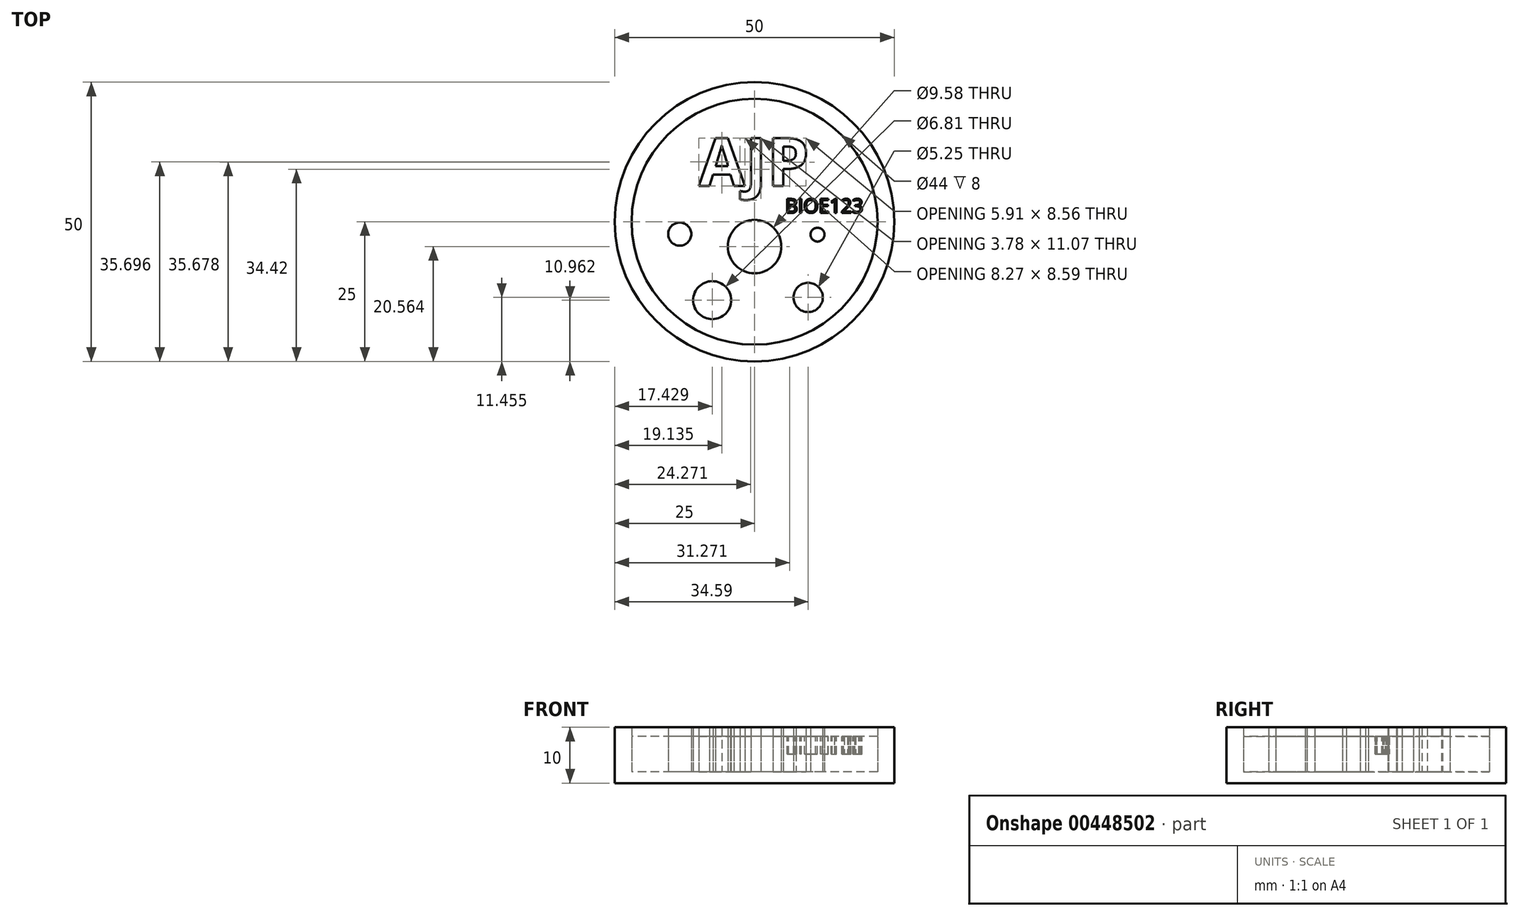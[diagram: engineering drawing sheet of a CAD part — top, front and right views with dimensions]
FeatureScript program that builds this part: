
annotation { "Feature Type Name" : "Feature", "Feature Type Description" : "" }
export const myFeature = defineFeature(function(context is Context, id is Id, definition is map)
    precondition{}
    {
        {
            var Q0;
            Q0=qCreatedBy(makeId("Top.planeOp"),FACE);
            var sketch = newSketch(context, id + "F0", { "sketchPlane" : qUnion([Q0])});
            skCircle(sketch, "E0", {"center": v(0, 0) * mm, "radius": 25 * mm});
            skCircle(sketch, "E1", {"center": v(0, 0) * mm, "radius": 22 * mm});
            skCircle(sketch, "E2", {"center": v(0, -4.44) * mm, "radius": 4.79 * mm});
            skCircle(sketch, "E3", {"center": v(-7.57, -14.04) * mm, "radius": 3.4 * mm});
            skCircle(sketch, "E4", {"center": v(9.6, -13.55) * mm, "radius": 2.63 * mm});
            skCircle(sketch, "E5", {"center": v(-13.39, -2.2) * mm, "radius": 2.07 * mm});
            skCircle(sketch, "E6", {"center": v(11.27, -2.3) * mm, "radius": 1.24 * mm});
            skSolve(sketch);
        }
        {
            var Q0;
            Q0=makeQuery(id+"F0.imprint","IMPRINT",FACE,{"disambiguationData":[TD([[makeQuery(id+"F0.imprint","IMPRINT",EDGE,{"derivedFrom":sQuery(id+"F0.wireOp",EDGE,"E0")}),1.0]])]});
            extrude(context, id + "F1", {"entities" : qUnion([Q0]), "depth" : 10 * mm});
        }
        {
            var Q0;
            Q0=makeQuery(id+"F0.imprint","IMPRINT",FACE,{"disambiguationData":[TD([[makeQuery(id+"F0.imprint","IMPRINT",EDGE,{"derivedFrom":sQuery(id+"F0.wireOp",EDGE,"E1")}),1.0]])]});
            extrude(context, id + "F2", {"entities" : qUnion([Q0]), "operationType" : NewBodyOperationType.ADD, "depth" : 2 * mm});
        }
        {
            var Q0;
            Q0=makeQuery(id+"F0.imprint","IMPRINT",FACE,{"disambiguationData":[TD([[makeQuery(id+"F0.imprint","IMPRINT",EDGE,{"derivedFrom":sQuery(id+"F0.wireOp",EDGE,"E5")}),1.0]])]});
            var Q1;
            Q1=makeQuery(id+"F0.imprint","IMPRINT",FACE,{"disambiguationData":[TD([[makeQuery(id+"F0.imprint","IMPRINT",EDGE,{"derivedFrom":sQuery(id+"F0.wireOp",EDGE,"E3")}),1.0]])]});
            var Q2;
            Q2=makeQuery(id+"F0.imprint","IMPRINT",FACE,{"disambiguationData":[TD([[makeQuery(id+"F0.imprint","IMPRINT",EDGE,{"derivedFrom":sQuery(id+"F0.wireOp",EDGE,"E2")}),1.0]])]});
            var Q3;
            Q3=makeQuery(id+"F0.imprint","IMPRINT",FACE,{"disambiguationData":[TD([[makeQuery(id+"F0.imprint","IMPRINT",EDGE,{"derivedFrom":sQuery(id+"F0.wireOp",EDGE,"E6")}),1.0]])]});
            var Q4;
            Q4=makeQuery(id+"F0.imprint","IMPRINT",FACE,{"disambiguationData":[TD([[makeQuery(id+"F0.imprint","IMPRINT",EDGE,{"derivedFrom":sQuery(id+"F0.wireOp",EDGE,"E4")}),1.0]])]});
            extrude(context, id + "F3", {"entities" : qUnion([Q0, Q1, Q2, Q3, Q4]), "operationType" : NewBodyOperationType.ADD, "depth" : 10 * mm});
        }
        {
            var Q0;
            Q0=qCreatedBy(makeId("Top.planeOp"),FACE);
            var sketch = newSketch(context, id + "F4", { "sketchPlane" : qUnion([Q0])});
            skText(sketch, "E7", { "text": "AJP", "fontName": "OpenSans-Bold.ttf"});
            const initialGuessF4  = {"E7": [-0.01, 0.0064, 1, 0, 0.00863]};
            skSetInitialGuess(sketch, initialGuessF4);
            skSolve(sketch);
        }
        {
            var Q0;
            Q0 = qSketchRegion(id + "F4", true);
            extrude(context, id + "F5", {"entities" : qUnion([Q0]), "operationType" : NewBodyOperationType.ADD, "depth" : 10 * mm});
        }
        {
            var Q0;
            {var subQ0=sQuery(id+"F0.wireOp",EDGE,"E6");var subQ1=sQuery(id+"F0.wireOp",EDGE,"E4");var subQ2=sQuery(id+"F0.wireOp",EDGE,"E3");var subQ3=sQuery(id+"F0.wireOp",EDGE,"E2");var subQ4=sQuery(id+"F0.wireOp",EDGE,"E1");var subQ5=sQuery(id+"F0.wireOp",EDGE,"E5");Q0=makeQuery(id+"F5.boolean.opBoolean","SPLIT",FACE,{"disambiguationData":[TD([makeQuery(id+"F1.opExtrude","SWEPT_FACE",FACE,{"disambiguationData":[OSD([subQ4])]})])],"derivedFrom":makeQuery(id+"F2.opExtrude","CAP_FACE",FACE,{"disambiguationData":[OSD([subQ4,subQ3,subQ2,subQ1,subQ5,subQ0])],"isStart":false})});}
            extrude(context, id + "F6", {"entities" : qUnion([Q0]), "depth" : 6.35 * mm});
        }
        {
            var Q0;
            Q0=makeQuery(id+"F6.opExtrude","CAP_FACE",FACE,{"disambiguationData":[OSD([sQuery(id+"F0.wireOp",EDGE,"E1"),sQuery(id+"F0.wireOp",EDGE,"E2"),sQuery(id+"F0.wireOp",EDGE,"E3"),sQuery(id+"F0.wireOp",EDGE,"E4"),sQuery(id+"F0.wireOp",EDGE,"E5"),sQuery(id+"F0.wireOp",EDGE,"E6")])],"isStart":false});
            var sketch = newSketch(context, id + "F7", { "sketchPlane" : qUnion([Q0])});
            skText(sketch, "E8", { "text": "BIOE123\n", "fontName": "OpenSans-Regular.ttf"});
            const initialGuessF7  = {"E8": [0.00547, 0.00159, 1, 0, 0.00253]};
            skSetInitialGuess(sketch, initialGuessF7);
            skSolve(sketch);
        }
        {
            var Q0;
            Q0 = qSketchRegion(id + "F7", true);
            extrude(context, id + "F8", {"entities" : qUnion([Q0]), "operationType" : NewBodyOperationType.REMOVE, "oppositeDirection" : true, "depth" : 3.17 * mm});
        }
    });
